# Revit family: Car structure.0002 2022
name_source: partatom
category: Generic Models
units: mm (PartAtom-declared; Revit-internal decimal feet)

## family parameters
Always vertical = Yes
Can host rebar = No
Cut with Voids When Loaded = No
Maintain Annotation Orientation = No
Part Type = Normal
Room Calculation Point = No
Round Connector Dimension = Use Diameter
Shared = No
Work Plane-Based = No

## types (1)
- Car structure.0002 2022
    BarrierFreeAccessibility = Yes
    Brand Name = BCA
    CapacityPeople = 13
    Car_Mass = 1080
    ClearDepth = 1750 mm  [stored 5.74147 ft]
    ClearHeight = 2990 mm
    ClearWidth = 2000 mm  [stored 6.56168 ft]
    ControlDevice_OperableDistance = 500
    Default Elevation = 0 mm  [stored 0 ft]
    Entrance = 1100 mm
    Entrance Height = 2100 mm
    Fire Safety Provision = Yes
    Lift Car Opening Depth = 200 mm  [stored 0.656168 ft]
    Lift Car Wall Panel Thickness = 50 mm  [stored 0.164042 ft]
    Lift Number = PL1
    Lift Type = Passenger Lift, Fire Lift
    MaxDecorWeight = 200
    Model = BCA 990
    RatedLoad = 980
    RatedSpeed = 1.0 m/s
    RopeCount = 3
    SlungDirection = under slung
    TravelHeight = 25000 mm  [stored 82.021 ft]
    Weight Load Capacity = 2260
    car platform height = 10 mm  [stored 0.0328084 ft]
    car wall panel height = 3000 mm  [stored 9.84252 ft]
    overall depth = 2000 mm  [stored 6.56168 ft]
    overall width = 2100 mm

note: [stored X ft] marks values corroborated as IEEE doubles in the binary element streams (Revit-internal decimal feet)

## geometry (parser evidence)
native form markers: Sweep x3
no freeform markers — native parametric forms only
